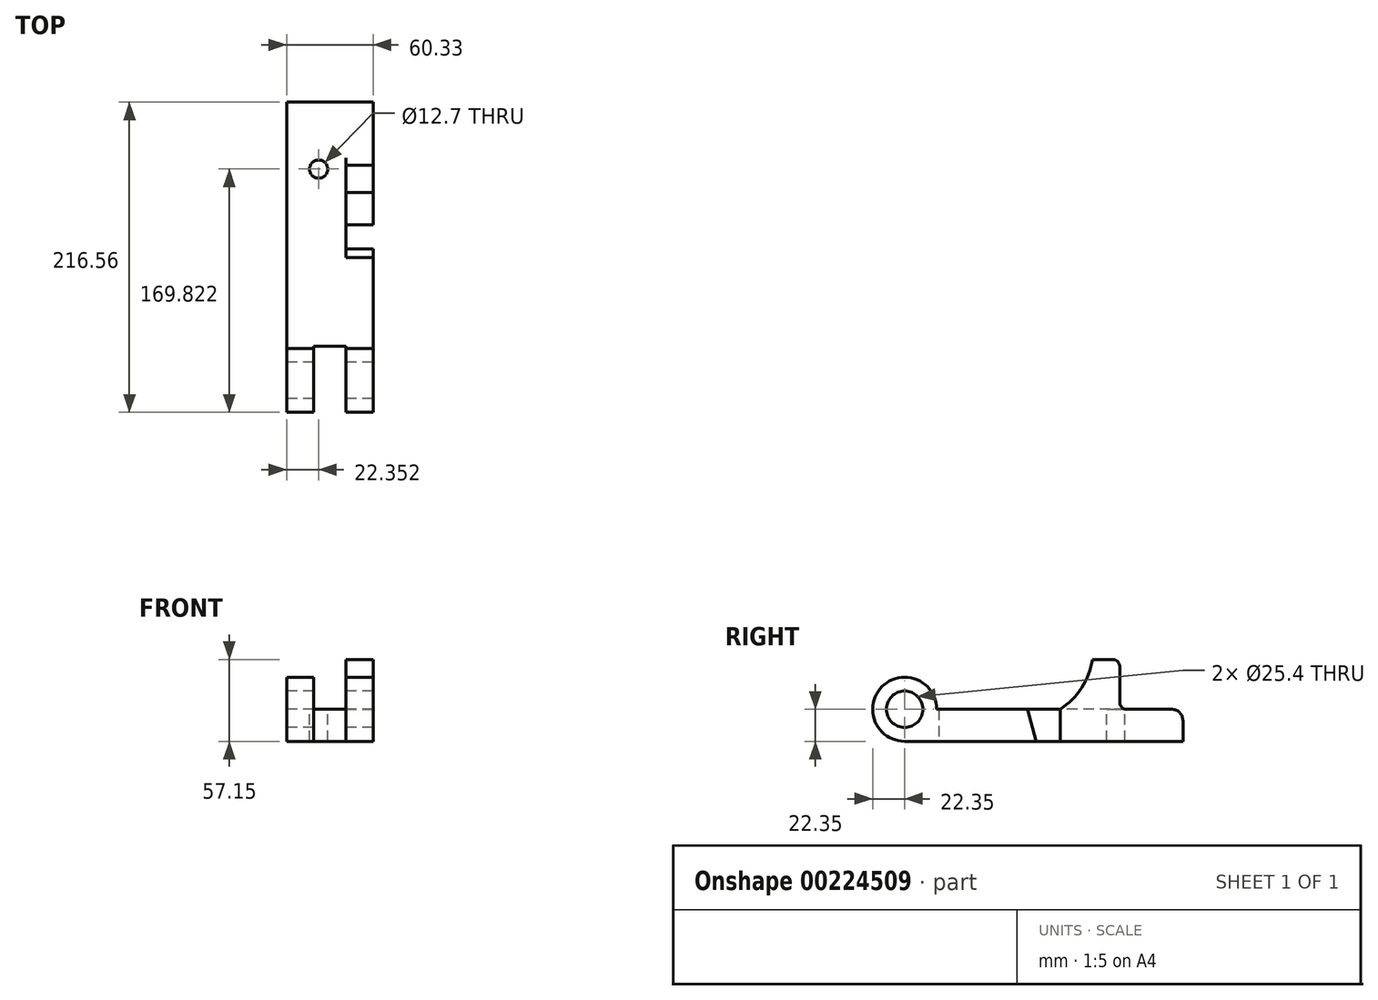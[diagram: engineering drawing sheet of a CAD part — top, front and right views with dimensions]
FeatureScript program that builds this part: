
annotation { "Feature Type Name" : "Feature", "Feature Type Description" : "" }
export const myFeature = defineFeature(function(context is Context, id is Id, definition is map)
    precondition{}
    {
        {
            var Q0;
            Q0=qCreatedBy(makeId("Right.planeOp"),FACE);
            var sketch = newSketch(context, id + "F0", { "sketchPlane" : qUnion([Q0])});
            skArc(sketch, "E0", {"start": v(22.35, 0) * mm, "mid": v(-15.8, 15.8) * mm, "end": v(0, -22.35) * mm});
            skLineSegment(sketch, "E1", {"start": v(0, -22.35) * mm, "end": v(194.2, -22.35) * mm});
            skLineSegment(sketch, "E2", {"start": v(0, 0) * mm, "end": v(-22.35, 0) * mm});
            skLineSegment(sketch, "E3", {"start": v(194.2, -22.35) * mm, "end": v(194.2, -7.87) * mm});
            skLineSegment(sketch, "E4", {"start": v(186.33, 0) * mm, "end": v(155.17, 0) * mm});
            skLineSegment(sketch, "E5", {"start": v(150.09, 5.08) * mm, "end": v(150.09, 29.72) * mm});
            skPoint(sketch, "E6.visualSharp", {"position": v(194.2, 0) * mm});
            skArc(sketch, "E6.filletArc", {"start": v(194.2, -7.87) * mm, "mid": v(191.9, -2.3) * mm, "end": v(186.33, 0) * mm});
            skLineSegment(sketch, "E7", {"start": v(145, 34.8) * mm, "end": v(131.04, 34.8) * mm});
            skLineSegment(sketch, "E8", {"start": v(108.5, 0) * mm, "end": v(22.35, 0) * mm});
            skArc(sketch, "E9", {"start": v(108.5, 0) * mm, "mid": v(123.48, 15) * mm, "end": v(131.04, 34.8) * mm});
            skPoint(sketch, "E10.visualSharp", {"position": v(150.09, 34.8) * mm});
            skArc(sketch, "E10.filletArc", {"start": v(150.09, 29.72) * mm, "mid": v(148.6, 33.31) * mm, "end": v(145, 34.8) * mm});
            skPoint(sketch, "E11.visualSharp", {"position": v(150.09, 0) * mm});
            skArc(sketch, "E11.filletArc", {"start": v(150.09, 5.08) * mm, "mid": v(151.58, 1.49) * mm, "end": v(155.17, 0) * mm});
            skSolve(sketch);
        }
        {
            var Q0;
            {var subQ3=sQuery(id+"F0.wireOp",EDGE,"E1");Q0=makeQuery(id+"F0.imprint","IMPRINT",FACE,{"disambiguationData":[TD([[makeQuery(id+"F0.imprint","IMPRINT",EDGE,{"derivedFrom":subQ3}),1.0]])]});}
            extrude(context, id + "F1", {"entities" : qUnion([Q0]), "depth" : 60.32 * mm});
        }
        {
            var Q0;
            Q0=makeQuery(id+"F1.opExtrude","CAP_FACE",FACE,{"disambiguationData":[OSD([sQuery(id+"F0.wireOp",EDGE,"E0"),sQuery(id+"F0.wireOp",EDGE,"E1"),sQuery(id+"F0.wireOp",EDGE,"E3"),sQuery(id+"F0.wireOp",EDGE,"E4"),sQuery(id+"F0.wireOp",EDGE,"E5"),sQuery(id+"F0.wireOp",EDGE,"E6.filletArc"),sQuery(id+"F0.wireOp",EDGE,"E7"),sQuery(id+"F0.wireOp",EDGE,"E8"),sQuery(id+"F0.wireOp",EDGE,"E9"),sQuery(id+"F0.wireOp",EDGE,"E10.filletArc"),sQuery(id+"F0.wireOp",EDGE,"E11.filletArc")])],"isStart":true});
            var sketch = newSketch(context, id + "F2", { "sketchPlane" : qUnion([Q0])});
            skLineSegment(sketch, "E12", {"start": v(-155.17, 0) * mm, "end": v(-108.5, 0) * mm});
            skArc(sketch, "E13", {"start": v(-131.04, 34.8) * mm, "mid": v(-123.48, 15) * mm, "end": v(-108.5, 0) * mm});
            skLineSegment(sketch, "E14", {"start": v(-150.09, 5.08) * mm, "end": v(-150.09, 29.72) * mm});
            skLineSegment(sketch, "E15", {"start": v(-145, 34.8) * mm, "end": v(-131.04, 34.8) * mm});
            skArc(sketch, "E16", {"start": v(-145, 34.8) * mm, "mid": v(-148.6, 33.31) * mm, "end": v(-150.09, 29.72) * mm});
            skArc(sketch, "E17", {"start": v(-155.17, 0) * mm, "mid": v(-151.58, 1.49) * mm, "end": v(-150.09, 5.08) * mm});
            skSolve(sketch);
        }
        {
            var Q0;
            Q0=makeQuery(id+"F2.imprint","IMPRINT",FACE,{"disambiguationData":[TD([[makeQuery(id+"F2.imprint","IMPRINT",EDGE,{"derivedFrom":sQuery(id+"F2.wireOp",EDGE,"E12")}),1.0]])]});
            extrude(context, id + "F3", {"entities" : qUnion([Q0]), "operationType" : NewBodyOperationType.REMOVE, "oppositeDirection" : true, "depth" : 41.33 * mm});
        }
        {
            var Q0;
            Q0=makeQuery(id+"F1.opExtrude","CAP_FACE",FACE,{"disambiguationData":[OSD([sQuery(id+"F0.wireOp",EDGE,"E0"),sQuery(id+"F0.wireOp",EDGE,"E1"),sQuery(id+"F0.wireOp",EDGE,"E3"),sQuery(id+"F0.wireOp",EDGE,"E4"),sQuery(id+"F0.wireOp",EDGE,"E5"),sQuery(id+"F0.wireOp",EDGE,"E6.filletArc"),sQuery(id+"F0.wireOp",EDGE,"E7"),sQuery(id+"F0.wireOp",EDGE,"E8"),sQuery(id+"F0.wireOp",EDGE,"E9"),sQuery(id+"F0.wireOp",EDGE,"E10.filletArc"),sQuery(id+"F0.wireOp",EDGE,"E11.filletArc")])],"isStart":false});
            var sketch = newSketch(context, id + "F4", { "sketchPlane" : qUnion([Q0])});
            skLineSegment(sketch, "E18", {"start": v(108.5, 0) * mm, "end": v(108.5, -22.35) * mm});
            skLineSegment(sketch, "E19", {"start": v(108.5, -22.35) * mm, "end": v(91.85, -22.35) * mm});
            skLineSegment(sketch, "E20", {"start": v(91.85, -22.35) * mm, "end": v(85.85, 0) * mm});
            skLineSegment(sketch, "E21", {"start": v(108.5, 0) * mm, "end": v(85.85, 0) * mm});
            skSolve(sketch);
        }
        {
            var Q0;
            Q0=makeQuery(id+"F4.imprint","IMPRINT",FACE,{"disambiguationData":[TD([[makeQuery(id+"F4.imprint","IMPRINT",EDGE,{"derivedFrom":sQuery(id+"F4.wireOp",EDGE,"E18")}),-1.0]])]});
            extrude(context, id + "F5", {"entities" : qUnion([Q0]), "operationType" : NewBodyOperationType.REMOVE, "oppositeDirection" : true, "depth" : 19.05 * mm});
        }
        {
            var Q0;
            Q0=makeQuery(id+"F3.boolean.opBoolean","MERGE",FACE,{"derivedFrom":[makeQuery(id+"F1.opExtrude","SWEPT_FACE",FACE,{"disambiguationData":[OSD([sQuery(id+"F0.wireOp",EDGE,"E4")])]}),makeQuery(id+"F1.opExtrude","SWEPT_FACE",FACE,{"disambiguationData":[OSD([sQuery(id+"F0.wireOp",EDGE,"E8")])]}),makeQuery(id+"F3.opExtrude","SWEPT_FACE",FACE,{"disambiguationData":[OSD([sQuery(id+"F2.wireOp",EDGE,"E12")])]})]});
            var sketch = newSketch(context, id + "F6", { "sketchPlane" : qUnion([Q0])});
            skLineSegment(sketch, "E22", {"start": v(0, 186.33) * mm, "end": v(0, 147.47) * mm, "construction": true});
            skLineSegment(sketch, "E23", {"start": v(0, 147.47) * mm, "end": v(22.35, 147.47) * mm, "construction": true});
            skCircle(sketch, "E24", {"center": v(22.35, 147.47) * mm, "radius": 6.35 * mm});
            skSolve(sketch);
        }
        {
            var Q0;
            Q0=makeQuery(id+"F6.imprint","IMPRINT",FACE,{"disambiguationData":[TD([[makeQuery(id+"F6.imprint","IMPRINT",EDGE,{"derivedFrom":sQuery(id+"F6.wireOp",EDGE,"E24")}),1.0]])]});
            extrude(context, id + "F7", {"entities" : qUnion([Q0]), "operationType" : NewBodyOperationType.REMOVE, "endBound" : BoundingType.THROUGH_ALL, "oppositeDirection" : true, "depth" : 25.4 * mm});
        }
        {
            var Q0;
            Q0=makeQuery(id+"F1.opExtrude","CAP_FACE",FACE,{"disambiguationData":[OSD([sQuery(id+"F0.wireOp",EDGE,"E0"),sQuery(id+"F0.wireOp",EDGE,"E1"),sQuery(id+"F0.wireOp",EDGE,"E3"),sQuery(id+"F0.wireOp",EDGE,"E4"),sQuery(id+"F0.wireOp",EDGE,"E5"),sQuery(id+"F0.wireOp",EDGE,"E6.filletArc"),sQuery(id+"F0.wireOp",EDGE,"E7"),sQuery(id+"F0.wireOp",EDGE,"E8"),sQuery(id+"F0.wireOp",EDGE,"E9"),sQuery(id+"F0.wireOp",EDGE,"E10.filletArc"),sQuery(id+"F0.wireOp",EDGE,"E11.filletArc")])],"isStart":true});
            var sketch = newSketch(context, id + "F8", { "sketchPlane" : qUnion([Q0])});
            skCircle(sketch, "E25", {"center": v(0, 0) * mm, "radius": 12.7 * mm});
            skSolve(sketch);
        }
        {
            var Q0;
            Q0=makeQuery(id+"F8.imprint","IMPRINT",FACE,{"disambiguationData":[TD([[makeQuery(id+"F8.imprint","IMPRINT",EDGE,{"derivedFrom":sQuery(id+"F8.wireOp",EDGE,"E25")}),1.0]])]});
            extrude(context, id + "F9", {"entities" : qUnion([Q0]), "operationType" : NewBodyOperationType.REMOVE, "endBound" : BoundingType.THROUGH_ALL, "oppositeDirection" : true, "depth" : 25.4 * mm});
        }
        {
            var Q0;
            Q0=makeQuery(id+"F1.opExtrude","SWEPT_FACE",FACE,{"disambiguationData":[OSD([sQuery(id+"F0.wireOp",EDGE,"E1")])]});
            var sketch = newSketch(context, id + "F10", { "sketchPlane" : qUnion([Q0])});
            skLineSegment(sketch, "E26", {"start": v(19, -23.78) * mm, "end": v(19, 22.46) * mm});
            skLineSegment(sketch, "E27", {"start": v(19, -23.78) * mm, "end": v(41.33, -23.78) * mm});
            skLineSegment(sketch, "E28", {"start": v(41.33, -23.78) * mm, "end": v(41.33, 22.46) * mm});
            skLineSegment(sketch, "E29", {"start": v(41.33, 22.46) * mm, "end": v(19, 22.46) * mm});
            skSolve(sketch);
        }
        {
            var Q0;
            {var subQ0=sQuery(id+"F10.wireOp",EDGE,"E29");Q0=makeQuery(id+"F10.imprint","IMPRINT",FACE,{"disambiguationData":[TD([[makeQuery(id+"F10.imprint","IMPRINT",EDGE,{"derivedFrom":subQ0}),1.0]])]});}
            var Q1;
            {var subQ0=sQuery(id+"F10.wireOp",EDGE,"E27");Q1=makeQuery(id+"F10.imprint","IMPRINT",FACE,{"disambiguationData":[TD([[makeQuery(id+"F10.imprint","IMPRINT",EDGE,{"derivedFrom":subQ0}),1.0]])]});}
            extrude(context, id + "F11", {"entities" : qUnion([Q0, Q1]), "operationType" : NewBodyOperationType.REMOVE, "endBound" : BoundingType.THROUGH_ALL, "oppositeDirection" : true, "depth" : 25.4 * mm});
        }
    });
